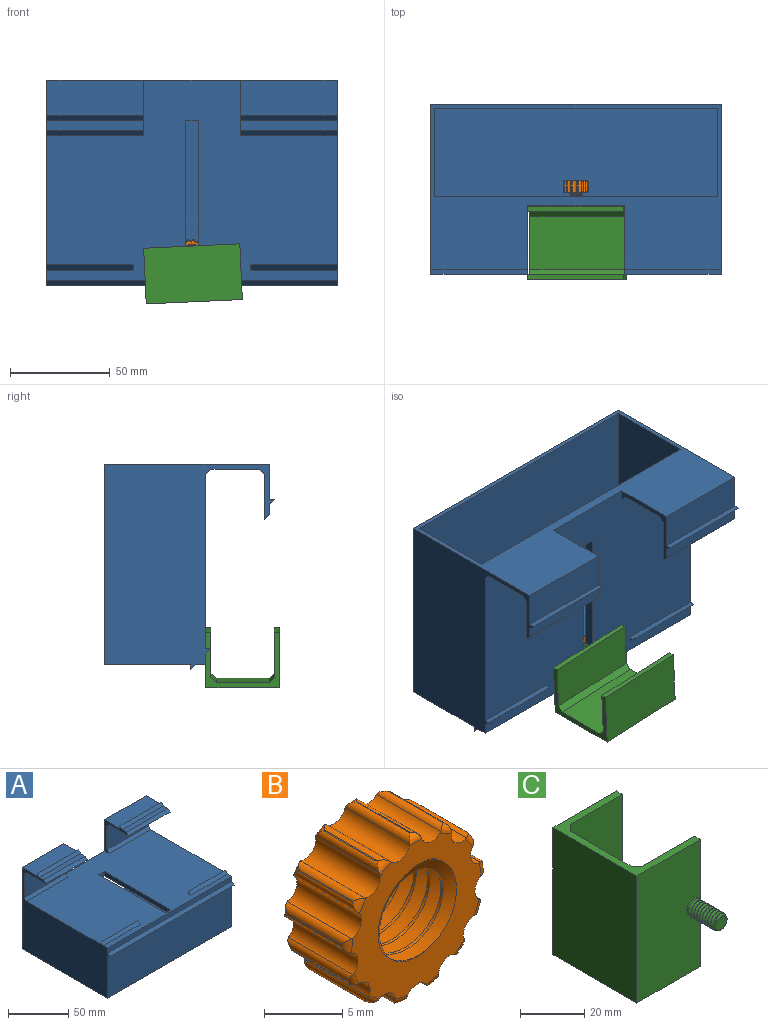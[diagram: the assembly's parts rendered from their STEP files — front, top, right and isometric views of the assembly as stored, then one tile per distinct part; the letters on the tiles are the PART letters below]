
ASSEMBLY  parts=3 mates=2
PART A: 43 faces, bbox 145.5x102.9x85.1 mm
  f0: plane 145.54x43.18mm, normal (0,-1,0), area 6284.5mm2, adj f12,f13,f14,f41
  f1: plane 145.54x100.33mm, normal (0,0,1), area 13395.6mm2, adj f4,f5,f6,f10,f11,f12,f13,f16
  f2: plane 48.51x17.78mm, normal (0,0,1), area 862.6mm2, adj f11,f13,f20,f32
  f3: plane 48.51x17.78mm, normal (0,0,1), area 862.6mm2, adj f11,f12,f17,f31
  f4: plane 77.85x4.57mm, normal (1,0,0), area 355.9mm2, adj f1,f6,f16,f28
  f5: plane 77.85x4.57mm, normal (-1,0,0), area 355.9mm2, adj f1,f6,f16,f28
  f6: plane 141.48x48.77mm, normal (0,1,0), area 6281.8mm2, adj f1,f4,f5,f7,f8,f15,f28
  f7: plane 98.3x44.2mm, normal (1,0,0), area 4344.4mm2, adj f6,f11,f15,f28
  f8: plane 98.3x44.2mm, normal (-1,0,0), area 4344.4mm2, adj f6,f11,f15,f28
  f9: plane 48.51x24.13mm, normal (0,-1,0), area 1170.6mm2, adj f12,f17,f24,f27
  f10: plane 145.54x5.08mm, normal (0,-1,0), area 739.4mm2, adj f1,f12,f13,f42
  f11: plane 145.54x82.55mm, normal (0,1,0), area 4221.4mm2, adj f1,f2,f3,f7,f8,f12,f13,f14
  f12: plane 102.87x85.09mm, normal (-1,0,0), area 5254.8mm2, adj f0,f1,f3,f9,f10,f11,f14,f18
  f13: plane 102.87x85.09mm, normal (1,0,0), area 5254.8mm2, adj f0,f1,f2,f10,f11,f14,f19,f21
  f14: plane 145.54x100.33mm, normal (0,0,-1), area 14602.2mm2, adj f0,f11,f12,f13
  f15: plane 141.48x98.3mm, normal (0,0,1), area 13907mm2, adj f6,f7,f8,f11
  f16: plane 6.35x4.57mm, normal (0,-1,0), area 29mm2, adj f1,f4,f5,f28
  f17: plane 34.29x27.94mm, normal (1,0,0), area 151.6mm2, adj f1,f3,f9,f11,f18,f22,f24,f27
  f18: plane 48.51x5.08mm, normal (0,0,1), area 246.5mm2, adj f12,f17,f29,f34
  f19: plane 48.51x24.13mm, normal (0,-1,0), area 1170.6mm2, adj f13,f20,f25,f26
  f20: plane 34.29x27.94mm, normal (-1,0,0), area 151.6mm2, adj f1,f2,f11,f19,f21,f23,f25,f26
  f21: plane 48.51x5.08mm, normal (0,0,1), area 246.5mm2, adj f13,f20,f30,f33
  f22: plane 48.51x22.86mm, normal (0,0,-1), area 1109mm2, adj f12,f17,f24,f29
  f23: plane 48.51x22.86mm, normal (0,0,-1), area 1109mm2, adj f13,f20,f25,f30
  f24: plane 48.51x2.54mm, normal (0,-0.71,-0.71), area 174.3mm2, adj f9,f12,f17,f22
  f25: plane 48.51x2.54mm, normal (0,-0.71,-0.71), area 174.3mm2, adj f13,f19,f20,f23
  f26: plane 48.51x2.54mm, normal (0,-0.71,0.71), area 174.3mm2, adj f1,f13,f19,f20
  f27: plane 48.51x2.54mm, normal (0,-0.71,0.71), area 174.3mm2, adj f1,f9,f12,f17
  f28: plane 141.48x98.3mm, normal (0,0,-1), area 13412.7mm2, adj f4,f5,f6,f7,f8,f11,f16
  f29: plane 48.51x2.54mm, normal (0,-0.71,0.71), area 174.3mm2, adj f12,f17,f18,f22
  f30: plane 48.51x2.54mm, normal (0,-0.71,0.71), area 174.3mm2, adj f13,f20,f21,f23
  f31: plane 48.51x2.54mm, normal (0,1,0), area 123.2mm2, adj f3,f12,f17,f34
  f32: plane 48.51x2.54mm, normal (0,1,0), area 123.2mm2, adj f2,f13,f20,f33
  f33: plane 48.51x2.54mm, normal (0,-0.71,0.71), area 174.3mm2, adj f13,f20,f21,f32
  f34: plane 48.51x2.54mm, normal (0,-0.71,0.71), area 174.3mm2, adj f12,f17,f18,f31
  f35: plane 2.54x2.54mm, normal (1,0,0), area 3.2mm2, adj f1,f36,f40
  f36: plane 43.18x2.54mm, normal (0,1,0), area 109.7mm2, adj f1,f12,f35,f40
  f37: plane 43.18x2.54mm, normal (0,1,0), area 109.7mm2, adj f1,f13,f38,f39
  f38: plane 2.54x2.54mm, normal (-1,0,0), area 3.2mm2, adj f1,f37,f39
  f39: plane 43.18x2.54mm, normal (0,-0.71,0.71), area 155.1mm2, adj f1,f13,f37,f38
  f40: plane 43.18x2.54mm, normal (0,-0.71,0.71), area 155.1mm2, adj f1,f12,f35,f36
  f41: plane 145.54x2.54mm, normal (0,0,-1), area 369.7mm2, adj f0,f12,f13,f42
  f42: plane 145.54x2.54mm, normal (0,-0.71,0.71), area 522.8mm2, adj f10,f12,f13,f41
PART B: 84 faces, bbox 13.4x7.7x13.3 mm
  f0: cylinder r=6.35mm len=4.83mm, axis (0,1,0), area 0.3mm2, adj f76,f77,f78,f79
  f1: cylinder r=6.35mm len=4.83mm, axis (0,1,0), area 0.3mm2, adj f80,f81,f82,f83
  f2: cylinder r=6.35mm len=4.83mm, axis (0,1,0), area 0.3mm2, adj f32,f33,f34,f35
  f3: cylinder r=6.35mm len=4.83mm, axis (0,1,0), area 0.3mm2, adj f36,f37,f38,f39
  f4: cylinder r=6.35mm len=4.83mm, axis (0,1,0), area 0.3mm2, adj f40,f41,f42,f43
  f5: cylinder r=6.35mm len=4.83mm, axis (0,1,0), area 0.3mm2, adj f44,f45,f46,f47
  f6: cylinder r=6.35mm len=4.83mm, axis (0,1,0), area 0.3mm2, adj f48,f49,f50,f51
  f7: cylinder r=6.35mm len=4.83mm, axis (0,1,0), area 0.3mm2, adj f52,f53,f54,f55
  f8: cylinder r=6.35mm len=4.83mm, axis (0,1,0), area 0.3mm2, adj f56,f57,f58,f59
  f9: cylinder r=6.35mm len=4.83mm, axis (0,1,0), area 0.3mm2, adj f60,f61,f62,f63
  f10: cylinder r=6.35mm len=4.83mm, axis (0,1,0), area 0.3mm2, adj f64,f65,f66,f67
  f11: cylinder r=6.35mm len=4.83mm, axis (0,1,0), area 0.3mm2, adj f68,f69,f70,f71
  f12: cylinder r=6.35mm len=4.83mm, axis (0,1,0), area 0.3mm2, adj f72,f73,f74,f75
  f13: bspline ~9.36x8.11mm, area 108.2mm2, adj f14,f15,f16,f30,f31
  f14: bspline ~9.36x8.11mm, area 108.1mm2, adj f13,f15,f16,f30,f31
  f15: cylinder r=3.17mm len=6.35mm, axis (0,-1,0), area 17.7mm2, adj f13,f14,f30,f31
  f16: plane 11.8x11.75mm, normal (0,1,0), area 55.3mm2, adj f13,f14,f17,f18,f19,f20,f21,f22
  f17: cylinder r=1.02mm len=5.84mm, axis (0,-1,0), area 13.2mm2, adj f16,f31,f72,f73,f75,f76,f78,f79
  f18: cylinder r=1.02mm len=5.84mm, axis (0,-1,0), area 13.2mm2, adj f16,f31,f68,f69,f71,f72,f74,f75
  f19: cylinder r=1.02mm len=5.84mm, axis (0,-1,0), area 13.2mm2, adj f16,f31,f64,f65,f67,f68,f70,f71
  f20: cylinder r=1.02mm len=5.84mm, axis (0,-1,0), area 13.2mm2, adj f16,f31,f60,f61,f63,f64,f66,f67
  f21: cylinder r=1.02mm len=5.84mm, axis (0,-1,0), area 13.2mm2, adj f16,f31,f56,f57,f59,f60,f62,f63
  f22: cylinder r=1.02mm len=5.84mm, axis (0,-1,0), area 13.2mm2, adj f16,f31,f52,f53,f55,f56,f58,f59
  f23: cylinder r=1.02mm len=5.84mm, axis (0,-1,0), area 13.2mm2, adj f16,f31,f48,f49,f51,f52,f54,f55
  f24: cylinder r=1.02mm len=5.84mm, axis (0,-1,0), area 13.2mm2, adj f16,f31,f44,f45,f47,f48,f50,f51
  f25: cylinder r=1.02mm len=5.84mm, axis (0,-1,0), area 13.2mm2, adj f16,f31,f40,f41,f43,f44,f46,f47
  f26: cylinder r=1.02mm len=5.84mm, axis (0,-1,0), area 13.2mm2, adj f16,f31,f36,f37,f39,f40,f42,f43
  f27: cylinder r=1.02mm len=5.84mm, axis (0,-1,0), area 13.2mm2, adj f16,f31,f32,f33,f35,f36,f38,f39
  f28: cylinder r=1.02mm len=5.84mm, axis (0,-1,0), area 13.2mm2, adj f16,f31,f32,f34,f35,f80,f81,f83
  f29: cylinder r=1.02mm len=5.84mm, axis (0,-1,0), area 13.2mm2, adj f16,f31,f76,f77,f79,f80,f82,f83
  f30: cone r=3.68mm half-angle=45deg, axis (0,1,0), area 6.4mm2, adj f13,f14,f15,f16
  f31: plane 12.28x12.23mm, normal (0,-1,0), area 59.8mm2, adj f13,f14,f15,f17,f18,f19,f20,f21
  f32: torus R=5.84mm, axis (0,-1,0), area 0.6mm2, adj f2,f16,f27,f28,f33,f34
  f33: cylinder r=0.51mm len=5.81mm, axis (0,1,0), area 3.7mm2, adj f2,f27,f32,f35
  f34: cylinder r=0.51mm len=5.81mm, axis (0,1,0), area 3.7mm2, adj f2,f28,f32,f35
  f35: torus R=5.84mm, axis (0,-1,0), area 0.6mm2, adj f2,f27,f28,f31,f33,f34
  f36: torus R=5.84mm, axis (0,-1,0), area 0.6mm2, adj f3,f16,f26,f27,f37,f38
  f37: cylinder r=0.51mm len=5.81mm, axis (0,1,0), area 3.7mm2, adj f3,f26,f36,f39
  f38: cylinder r=0.51mm len=5.81mm, axis (0,1,0), area 3.7mm2, adj f3,f27,f36,f39
  f39: torus R=5.84mm, axis (0,-1,0), area 0.6mm2, adj f3,f26,f27,f31,f37,f38
  f40: torus R=5.84mm, axis (0,-1,0), area 0.6mm2, adj f4,f16,f25,f26,f41,f42
  f41: cylinder r=0.51mm len=5.81mm, axis (0,1,0), area 3.7mm2, adj f4,f25,f40,f43
  f42: cylinder r=0.51mm len=5.81mm, axis (0,1,0), area 3.7mm2, adj f4,f26,f40,f43
  f43: torus R=5.84mm, axis (0,-1,0), area 0.6mm2, adj f4,f25,f26,f31,f41,f42
  f44: torus R=5.84mm, axis (0,-1,0), area 0.6mm2, adj f5,f16,f24,f25,f45,f46
  f45: cylinder r=0.51mm len=5.81mm, axis (0,1,0), area 3.7mm2, adj f5,f24,f44,f47
  f46: cylinder r=0.51mm len=5.81mm, axis (0,1,0), area 3.7mm2, adj f5,f25,f44,f47
  f47: torus R=5.84mm, axis (0,-1,0), area 0.6mm2, adj f5,f24,f25,f31,f45,f46
  f48: torus R=5.84mm, axis (0,-1,0), area 0.6mm2, adj f6,f16,f23,f24,f49,f50
  f49: cylinder r=0.51mm len=5.81mm, axis (0,1,0), area 3.7mm2, adj f6,f23,f48,f51
  f50: cylinder r=0.51mm len=5.81mm, axis (0,1,0), area 3.7mm2, adj f6,f24,f48,f51
  f51: torus R=5.84mm, axis (0,-1,0), area 0.6mm2, adj f6,f23,f24,f31,f49,f50
  f52: torus R=5.84mm, axis (0,-1,0), area 0.6mm2, adj f7,f16,f22,f23,f53,f54
  f53: cylinder r=0.51mm len=5.81mm, axis (0,1,0), area 3.7mm2, adj f7,f22,f52,f55
  f54: cylinder r=0.51mm len=5.81mm, axis (0,1,0), area 3.7mm2, adj f7,f23,f52,f55
  f55: torus R=5.84mm, axis (0,-1,0), area 0.6mm2, adj f7,f22,f23,f31,f53,f54
  f56: torus R=5.84mm, axis (0,-1,0), area 0.6mm2, adj f8,f16,f21,f22,f57,f58
  f57: cylinder r=0.51mm len=5.81mm, axis (0,1,0), area 3.7mm2, adj f8,f21,f56,f59
  f58: cylinder r=0.51mm len=5.81mm, axis (0,1,0), area 3.7mm2, adj f8,f22,f56,f59
  f59: torus R=5.84mm, axis (0,-1,0), area 0.6mm2, adj f8,f21,f22,f31,f57,f58
  f60: torus R=5.84mm, axis (0,-1,0), area 0.6mm2, adj f9,f16,f20,f21,f61,f62
  f61: cylinder r=0.51mm len=5.81mm, axis (0,1,0), area 3.7mm2, adj f9,f20,f60,f63
  f62: cylinder r=0.51mm len=5.81mm, axis (0,1,0), area 3.7mm2, adj f9,f21,f60,f63
  f63: torus R=5.84mm, axis (0,-1,0), area 0.6mm2, adj f9,f20,f21,f31,f61,f62
  f64: torus R=5.84mm, axis (0,-1,0), area 0.6mm2, adj f10,f16,f19,f20,f65,f66
  f65: cylinder r=0.51mm len=5.81mm, axis (0,1,0), area 3.7mm2, adj f10,f19,f64,f67
  f66: cylinder r=0.51mm len=5.81mm, axis (0,1,0), area 3.7mm2, adj f10,f20,f64,f67
  f67: torus R=5.84mm, axis (0,-1,0), area 0.6mm2, adj f10,f19,f20,f31,f65,f66
  f68: torus R=5.84mm, axis (0,-1,0), area 0.6mm2, adj f11,f16,f18,f19,f69,f70
  f69: cylinder r=0.51mm len=5.81mm, axis (0,1,0), area 3.7mm2, adj f11,f18,f68,f71
  f70: cylinder r=0.51mm len=5.81mm, axis (0,1,0), area 3.7mm2, adj f11,f19,f68,f71
  f71: torus R=5.84mm, axis (0,-1,0), area 0.6mm2, adj f11,f18,f19,f31,f69,f70
  f72: torus R=5.84mm, axis (0,-1,0), area 0.6mm2, adj f12,f16,f17,f18,f73,f74
  f73: cylinder r=0.51mm len=5.81mm, axis (0,1,0), area 3.7mm2, adj f12,f17,f72,f75
  f74: cylinder r=0.51mm len=5.81mm, axis (0,1,0), area 3.7mm2, adj f12,f18,f72,f75
  f75: torus R=5.84mm, axis (0,-1,0), area 0.6mm2, adj f12,f17,f18,f31,f73,f74
  f76: torus R=5.84mm, axis (0,-1,0), area 0.6mm2, adj f0,f16,f17,f29,f77,f78
  f77: cylinder r=0.51mm len=5.81mm, axis (0,1,0), area 3.7mm2, adj f0,f29,f76,f79
  f78: cylinder r=0.51mm len=5.81mm, axis (0,1,0), area 3.7mm2, adj f0,f17,f76,f79
  f79: torus R=5.84mm, axis (0,-1,0), area 0.6mm2, adj f0,f17,f29,f31,f77,f78
  f80: torus R=5.84mm, axis (0,-1,0), area 0.6mm2, adj f1,f16,f28,f29,f81,f82
  f81: cylinder r=0.51mm len=5.81mm, axis (0,1,0), area 3.7mm2, adj f1,f28,f80,f83
  f82: cylinder r=0.51mm len=5.81mm, axis (0,1,0), area 3.7mm2, adj f1,f29,f80,f83
  f83: torus R=5.84mm, axis (0,-1,0), area 0.6mm2, adj f1,f28,f29,f31,f81,f82
PART C: 18 faces, bbox 28.1x49.7x48.4 mm
  f0: plane 48.26x26.67mm, normal (1,0,0), area 1287.1mm2, adj f10,f12,f16,f17
  f1: plane 48.26x22.86mm, normal (0,1,0), area 1103.2mm2, adj f9,f10,f12,f17
  f2: cylinder r=3.05mm len=11.68mm, axis (0,1,0), area 30mm2, adj f4,f5,f6,f7,f8,f9
  f3: plane 5.23x4.97mm, normal (0,-1,0), area 19.3mm2, adj f4,f6,f7
  f4: cone r=2.54mm half-angle=45deg, axis (0,1,0), area 5mm2, adj f2,f3,f6,f7
  f5: plane 0.88x0.76mm, normal (0,0,-1), area 0.4mm2, adj f2,f6,f7,f8
  f6: bspline ~12.7x7.04mm, area 163.4mm2, adj f2,f3,f4,f5,f7,f8
  f7: bspline ~12.5x7.04mm, area 157.3mm2, adj f2,f3,f4,f5,f6
  f8: plane 48.4x28.08mm, normal (0,-1,0), area 1320mm2, adj f2,f5,f6,f9,f10,f11,f12
  f9: plane 48.26x2.54mm, normal (1,0,0), area 122.6mm2, adj f1,f2,f8,f10,f12
  f10: plane 36.83x27.94mm, normal (0,0,-1), area 229mm2, adj f0,f1,f8,f9,f11,f13,f14,f15
  f11: plane 48.26x36.83mm, normal (-1,0,0), area 1777.4mm2, adj f8,f10,f12,f13
  f12: plane 36.83x27.94mm, normal (0,0,1), area 229mm2, adj f0,f1,f8,f9,f11,f13,f14,f15
  f13: plane 48.26x27.94mm, normal (0,1,0), area 1348.4mm2, adj f10,f11,f12,f15
  f14: plane 48.26x22.86mm, normal (0,-1,0), area 1103.2mm2, adj f10,f12,f15,f16
  f15: plane 48.26x2.54mm, normal (1,0,0), area 122.6mm2, adj f10,f12,f13,f14
  f16: plane 48.26x2.54mm, normal (0.71,-0.71,0), area 173.4mm2, adj f0,f10,f12,f14
  f17: plane 48.26x2.54mm, normal (0.71,0.71,0), area 173.4mm2, adj f0,f1,f10,f12
PLACE A rot(axis=(1,0,0),90deg) t=(-2.2,-41.29,77.42)mm fixed
PLACE B rot(axis=(0,-1,0),17.2deg) t=(-36.39,-79.41,37.98)mm
PLACE C rot(axis=(-0.69,0,-0.72),180deg) t=(-36.18,-92.09,37.94)mm
MATE pin_slot C.f2 <-> A.f1  axis (0,1,0) through (-36.18,-92.09,37.94)mm
MATE cylindrical B.f16 <-> C.f3  axis (0,1,0) through (-36.29,-79.41,37.96)mm
